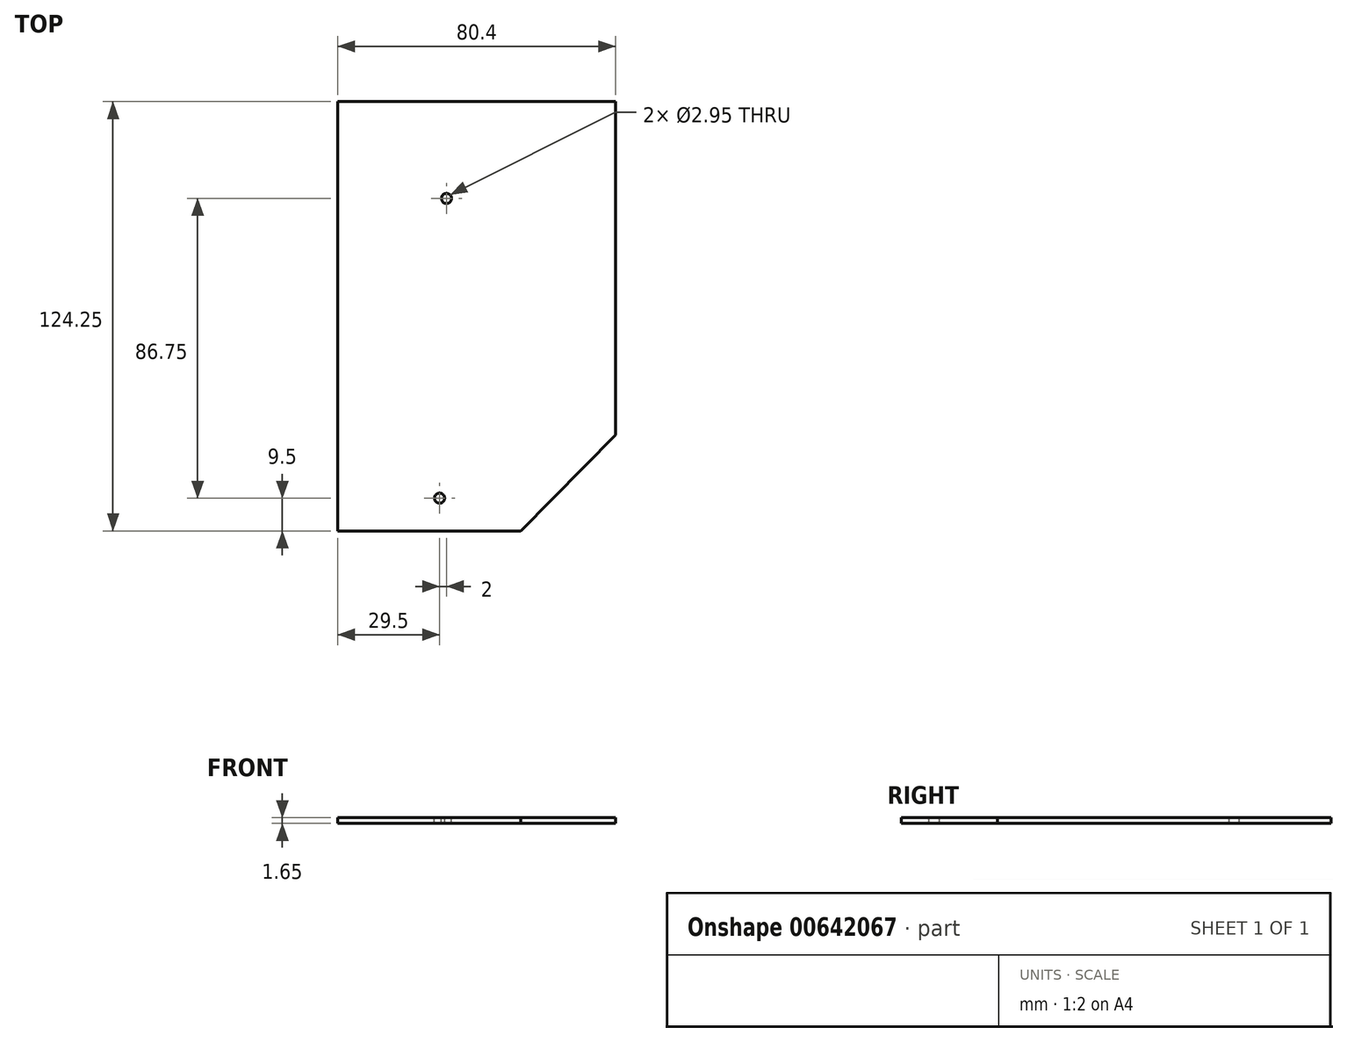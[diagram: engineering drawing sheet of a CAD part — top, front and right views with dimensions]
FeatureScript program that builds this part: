
annotation { "Feature Type Name" : "Feature", "Feature Type Description" : "" }
export const myFeature = defineFeature(function(context is Context, id is Id, definition is map)
    precondition{}
    {
        {
            var Q0;
            Q0=qCreatedBy(makeId("Top.planeOp"),FACE);
            var sketch = newSketch(context, id + "F0", { "sketchPlane" : qUnion([Q0])});
            skLineSegment(sketch, "E0.bottom", {"start": v(0, 0) * mm, "end": v(80.4, 0) * mm});
            skLineSegment(sketch, "E0.top", {"start": v(0, 124.25) * mm, "end": v(80.4, 124.25) * mm});
            skLineSegment(sketch, "E0.left", {"start": v(0, 0) * mm, "end": v(0, 124.25) * mm});
            skLineSegment(sketch, "E0.right", {"start": v(80.4, 0) * mm, "end": v(80.4, 124.25) * mm});
            skSolve(sketch);
        }
        {
            var Q0;
            Q0 = qSketchRegion(id + "F0", true);
            extrude(context, id + "F1", {"entities" : qUnion([Q0]), "depth" : 1.65 * mm, "offsetDistance" : 25 * mm});
        }
        {
            var Q0;
            Q0=makeQuery(id+"F1.opExtrude","CAP_FACE",FACE,{"disambiguationData":[OSD([sQuery(id+"F0.wireOp",EDGE,"E0.bottom"),sQuery(id+"F0.wireOp",EDGE,"E0.top"),sQuery(id+"F0.wireOp",EDGE,"E0.left"),sQuery(id+"F0.wireOp",EDGE,"E0.right")])],"isStart":false});
            var sketch = newSketch(context, id + "F2", { "sketchPlane" : qUnion([Q0])});
            skLineSegment(sketch, "E1", {"start": v(80.4, 27.75) * mm, "end": v(53, 0) * mm});
            skLineSegment(sketch, "E2", {"start": v(53, 0) * mm, "end": v(80.4, 0) * mm});
            skLineSegment(sketch, "E3", {"start": v(80.4, 0) * mm, "end": v(80.4, 27.75) * mm});
            skSolve(sketch);
        }
        {
            var Q0;
            Q0 = qSketchRegion(id + "F2", true);
            extrude(context, id + "F3", {"entities" : qUnion([Q0]), "operationType" : NewBodyOperationType.REMOVE, "endBound" : BoundingType.THROUGH_ALL, "oppositeDirection" : true, "depth" : 25 * mm, "offsetDistance" : 25 * mm});
        }
        {
            var Q0;
            Q0=makeQuery(id+"F1.opExtrude","CAP_FACE",FACE,{"disambiguationData":[OSD([sQuery(id+"F0.wireOp",EDGE,"E0.bottom"),sQuery(id+"F0.wireOp",EDGE,"E0.top"),sQuery(id+"F0.wireOp",EDGE,"E0.left"),sQuery(id+"F0.wireOp",EDGE,"E0.right")])],"isStart":false});
            var sketch = newSketch(context, id + "F4", { "sketchPlane" : qUnion([Q0])});
            skPoint(sketch, "E4", {"position": v(31.5, 96.25) * mm});
            skPoint(sketch, "E5", {"position": v(29.5, 9.5) * mm});
            skSolve(sketch);
        }
        {
            var Q0;
            Q0=sQuery(id+"F4.wireOp",VERTEX,"E4");
            var Q1;
            Q1=sQuery(id+"F4.wireOp",VERTEX,"E5");
            var Q2;
            Q2=makeQuery(id+"F1.opExtrude","SWEPT_BODY",BODY,{"disambiguationData":[OSD([sQuery(id+"F0.wireOp",EDGE,"E0.bottom"),sQuery(id+"F0.wireOp",EDGE,"E0.top"),sQuery(id+"F0.wireOp",EDGE,"E0.left"),sQuery(id+"F0.wireOp",EDGE,"E0.right")])]});
            hole(context, id + "F5", {"style" : HoleStyle.SIMPLE, "endStyle" : HoleEndStyle.THROUGH, "standardTappedOrClearance" : lookupTablePath({ "standard" : "ANSI", "fit" : "Close", "size" : "#4", "type" : "Clearance" }), "standardBlindInLast" : lookupTablePath({ "fit" : "Close", "standard" : "ANSI", "size" : "#4", "type" : "Clearance" }), "holeDiameter" : 2.95 * mm, "majorDiameter" : 5 * mm, "isTappedThrough" : true, "tappedDepth" : 12 * mm, "tapClearance" : 3, "startFromSketch" : true, "locations" : qUnion([Q0, Q1]), "scope" : qUnion([Q2])});
        }
    });
